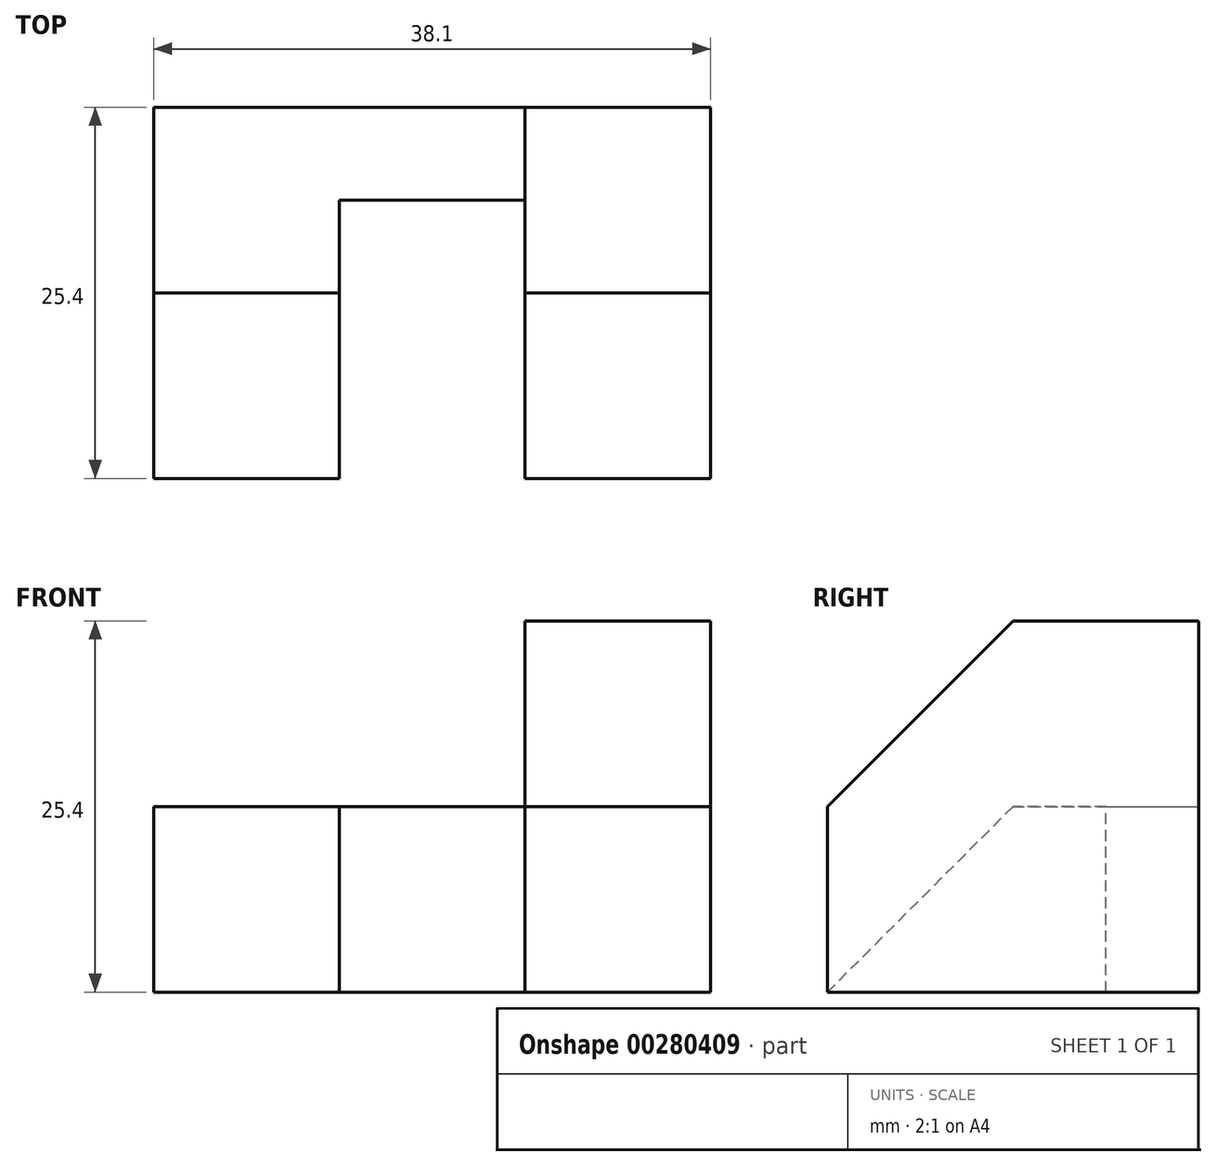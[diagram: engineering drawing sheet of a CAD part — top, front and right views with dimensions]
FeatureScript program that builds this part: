
annotation { "Feature Type Name" : "Feature", "Feature Type Description" : "" }
export const myFeature = defineFeature(function(context is Context, id is Id, definition is map)
    precondition{}
    {
        {
            var Q0;
            Q0=qCreatedBy(makeId("Front.planeOp"),FACE);
            var sketch = newSketch(context, id + "F0", { "sketchPlane" : qUnion([Q0])});
            skLineSegment(sketch, "E0", {"start": v(0, 0) * mm, "end": v(0, 25.4) * mm});
            skLineSegment(sketch, "E1", {"start": v(0, 25.4) * mm, "end": v(38.1, 25.4) * mm});
            skLineSegment(sketch, "E2", {"start": v(38.1, 25.4) * mm, "end": v(38.1, 0) * mm});
            skLineSegment(sketch, "E3", {"start": v(38.1, 0) * mm, "end": v(0, 0) * mm});
            skSolve(sketch);
        }
        {
            var Q0;
            Q0 = qSketchRegion(id + "F0", true);
            extrude(context, id + "F1", {"entities" : qUnion([Q0]), "depth" : 25.4 * mm});
        }
        {
            var Q0;
            Q0=makeQuery(id+"F1.opExtrude","SWEPT_FACE",FACE,{"disambiguationData":[OSD([sQuery(id+"F0.wireOp",EDGE,"E2")])]});
            var sketch = newSketch(context, id + "F2", { "sketchPlane" : qUnion([Q0])});
            skLineSegment(sketch, "E4", {"start": v(-25.4, 12.7) * mm, "end": v(-12.7, 25.4) * mm});
            skLineSegment(sketch, "E5", {"start": v(-12.7, 25.4) * mm, "end": v(-25.4, 25.4) * mm});
            skLineSegment(sketch, "E6", {"start": v(-25.4, 25.4) * mm, "end": v(-25.4, 12.7) * mm});
            skSolve(sketch);
        }
        {
            var Q0;
            Q0 = qSketchRegion(id + "F2", true);
            extrude(context, id + "F3", {"entities" : qUnion([Q0]), "operationType" : NewBodyOperationType.REMOVE, "oppositeDirection" : true, "depth" : 12.7 * mm});
        }
        {
            var Q0;
            Q0=makeQuery(id+"F1.opExtrude","SWEPT_FACE",FACE,{"disambiguationData":[OSD([sQuery(id+"F0.wireOp",EDGE,"E1")])]});
            var sketch = newSketch(context, id + "F4", { "sketchPlane" : qUnion([Q0])});
            skLineSegment(sketch, "E7", {"start": v(12.7, -12.7) * mm, "end": v(12.7, -6.35) * mm});
            skPoint(sketch, "E7.startSnap0", {"position": v(0, -12.7) * mm});
            skLineSegment(sketch, "E8", {"start": v(12.7, -6.35) * mm, "end": v(25.4, -6.35) * mm});
            skLineSegment(sketch, "E9", {"start": v(25.4, -6.35) * mm, "end": v(25.4, -12.7) * mm});
            skLineSegment(sketch, "E10", {"start": v(25.4, -12.7) * mm, "end": v(12.7, -12.7) * mm});
            skLineSegment(sketch, "E11", {"start": v(12.7, -12.7) * mm, "end": v(12.7, -25.4) * mm});
            skLineSegment(sketch, "E12", {"start": v(12.7, -25.4) * mm, "end": v(25.4, -25.4) * mm});
            skLineSegment(sketch, "E13", {"start": v(25.4, -25.4) * mm, "end": v(25.4, -12.7) * mm});
            skSolve(sketch);
        }
        {
            var Q0;
            Q0 = qSketchRegion(id + "F4", true);
            extrude(context, id + "F5", {"entities" : qUnion([Q0]), "operationType" : NewBodyOperationType.REMOVE, "oppositeDirection" : true, "depth" : 25.4 * mm});
        }
        {
            var Q0;
            Q0=makeQuery(id+"F1.opExtrude","SWEPT_FACE",FACE,{"disambiguationData":[OSD([sQuery(id+"F0.wireOp",EDGE,"E0")])]});
            var sketch = newSketch(context, id + "F6", { "sketchPlane" : qUnion([Q0])});
            skLineSegment(sketch, "E14", {"start": v(0, 25.4) * mm, "end": v(12.7, 25.4) * mm});
            skLineSegment(sketch, "E15", {"start": v(12.7, 25.4) * mm, "end": v(12.7, 12.7) * mm});
            skLineSegment(sketch, "E16", {"start": v(12.7, 12.7) * mm, "end": v(0, 12.7) * mm});
            skLineSegment(sketch, "E17", {"start": v(0, 12.7) * mm, "end": v(0, 25.4) * mm});
            skSolve(sketch);
        }
        {
            var Q0;
            Q0 = qSketchRegion(id + "F6", true);
            extrude(context, id + "F7", {"entities" : qUnion([Q0]), "operationType" : NewBodyOperationType.REMOVE, "oppositeDirection" : true, "depth" : 25.4 * mm});
        }
        {
            var Q0;
            Q0=makeQuery(id+"F1.opExtrude","SWEPT_FACE",FACE,{"disambiguationData":[OSD([sQuery(id+"F0.wireOp",EDGE,"E0")])]});
            var sketch = newSketch(context, id + "F8", { "sketchPlane" : qUnion([Q0])});
            skLineSegment(sketch, "E18", {"start": v(12.7, 12.7) * mm, "end": v(25.4, 0) * mm});
            skLineSegment(sketch, "E19", {"start": v(25.4, 0) * mm, "end": v(25.4, 25.4) * mm});
            skLineSegment(sketch, "E20", {"start": v(25.4, 25.4) * mm, "end": v(12.7, 25.4) * mm});
            skLineSegment(sketch, "E21", {"start": v(12.7, 25.4) * mm, "end": v(12.7, 12.7) * mm});
            skSolve(sketch);
        }
        {
            var Q0;
            Q0 = qSketchRegion(id + "F8", true);
            extrude(context, id + "F9", {"entities" : qUnion([Q0]), "operationType" : NewBodyOperationType.REMOVE, "oppositeDirection" : true, "depth" : 25.4 * mm});
        }
    });
